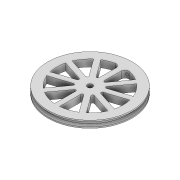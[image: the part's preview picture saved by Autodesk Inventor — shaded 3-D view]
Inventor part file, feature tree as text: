
AUTODESK INVENTOR PART (.ipt)
format: ipt  version: 2022 (Build 260153000, 153)  size: 373,248 bytes
history: native  units: mm
features: extrude x6, sketch x6, plane x2, fillet x2, projected_geometry x2
ambient origin geometry x8: Origin, YZ Plane, XZ Plane, XY Plane, X Axis, Y Axis, Z Axis, Center Point
bodies: Solid1 (feature_tree)
feature tree (18):
  extrude  "Extrusion1"  Depth=60.0mm
  extrude  "Extrusion13"  Depth=3.5mm TaperAngle=0.0deg
  plane  "Work Plane8"
  plane  "Work Plane9"
  sketch  "Sketch14"  dims[d81=3.0mm d87=4.0mm]
  sketch  "Sketch15"  dims[d88=2.0mm d92=100.0mm d94=360.0deg]
  fillet  "Fillet4"  Radius=52.0mm
  fillet  "Fillet5"  Radius=10.0mm
  extrude  "Extrusion14"  Depth=3.0mm
  extrude  "Extrusion15"  Depth=2.0mm TaperAngle=360.0deg
  extrude  "Extrusion16"  Depth=1.0mm
  extrude  "Extrusion17"  Depth=1.0mm
  sketch  "Sketch1"  dims[d0=4.1mm d2=60.0mm]
  sketch  "Sketch11"  dims[d3=4.0mm d4=3.5mm d5=0.0mm d76=52.0mm d79=10.0mm d80=0.0mm]
  sketch  "Sketch16"  dims[d96=3.0mm d97=1.0mm]
  sketch  "Sketch18"  dims[d101=-6.981317mm d102=6.981317mm d103=2.2mm d104=1.75mm d105=2.2mm d106=1.75mm d107=10.0mm d108=0.0mm d109=10.0mm d110=0.0mm d111=1.5mm d112=1.5mm d114=3.0mm d115=1.0mm d116=0.0mm d117=3.0mm d118=1.0mm d119=0.0mm]
  projected_geometry  "Projected Loop5"
  projected_geometry  "Projected Loop6"
